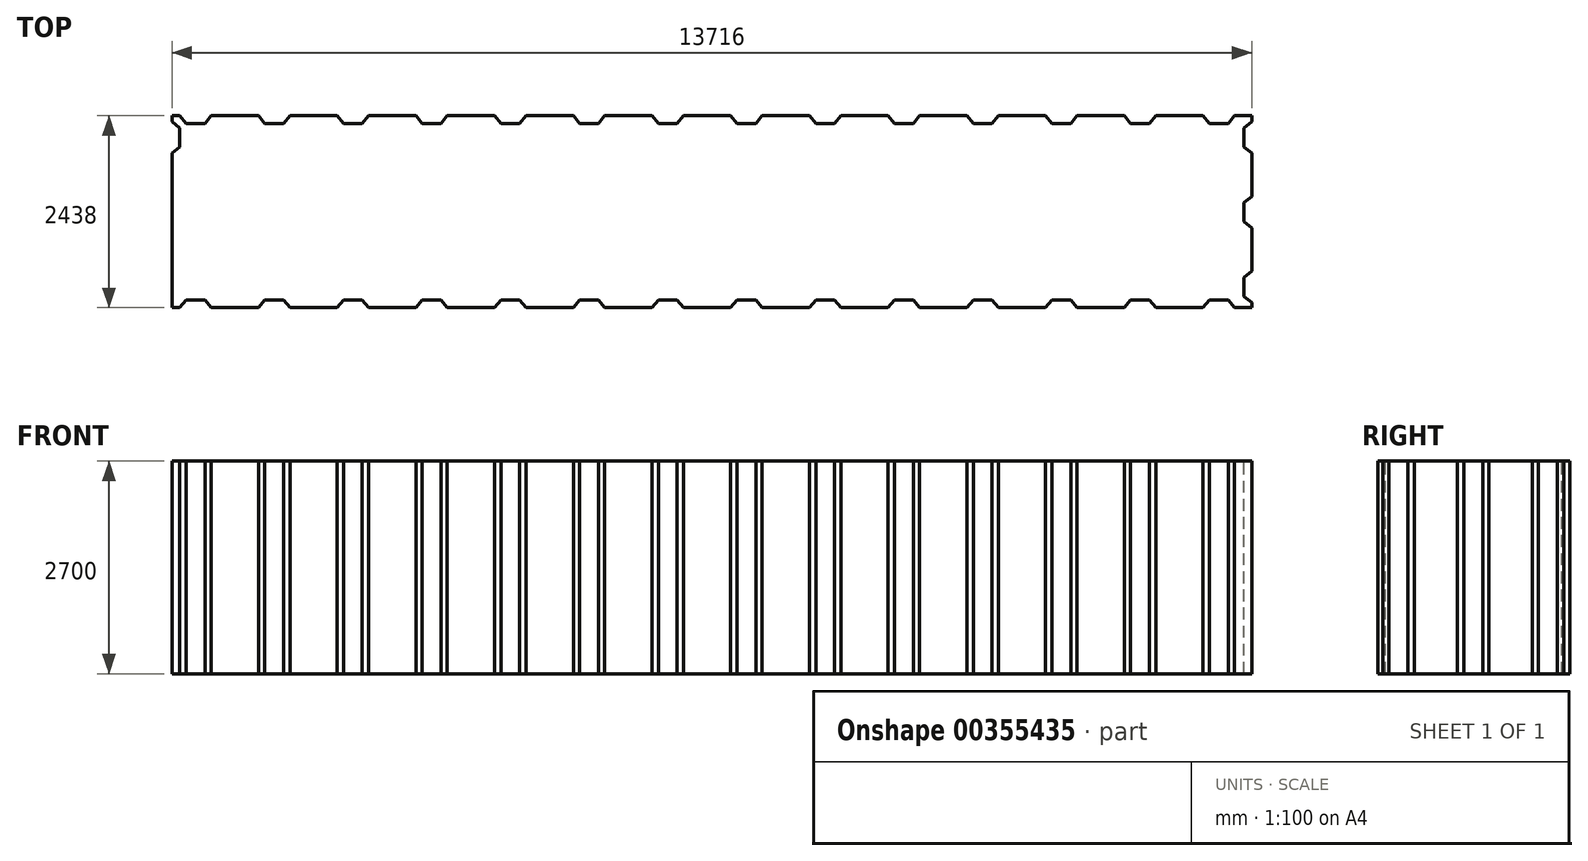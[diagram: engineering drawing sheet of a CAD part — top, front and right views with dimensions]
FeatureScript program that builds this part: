
annotation { "Feature Type Name" : "Feature", "Feature Type Description" : "" }
export const myFeature = defineFeature(function(context is Context, id is Id, definition is map)
    precondition{}
    {
        {
            var Q0;
            Q0=qCreatedBy(makeId("Top.planeOp"),FACE);
            var sketch = newSketch(context, id + "F0", { "sketchPlane" : qUnion([Q0])});
            skLineSegment(sketch, "E0.bottom", {"start": v(6858, -1219) * mm, "end": v(-6858, -1219) * mm});
            skLineSegment(sketch, "E0.top", {"start": v(6858, 1219) * mm, "end": v(-6858, 1219) * mm});
            skLineSegment(sketch, "E0.left", {"start": v(6858, -1219) * mm, "end": v(6858, 1219) * mm});
            skLineSegment(sketch, "E0.right", {"start": v(-6858, -1219) * mm, "end": v(-6858, 1219) * mm});
            skPoint(sketch, "E0.middle", {"position": v(0, 0) * mm});
            skSolve(sketch);
        }
        {
            var Q0;
            Q0=makeQuery(id+"F0.imprint","IMPRINT",FACE,{"disambiguationData":[TD([[makeQuery(id+"F0.imprint","IMPRINT",EDGE,{"derivedFrom":sQuery(id+"F0.wireOp",EDGE,"E0.bottom")}),-1.0]])]});
            extrude(context, id + "F1", {"entities" : qUnion([Q0]), "depth" : 2700 * mm});
        }
        {
            var Q0;
            Q0=makeQuery(id+"F1.opExtrude","CAP_FACE",FACE,{"disambiguationData":[OSD([sQuery(id+"F0.wireOp",EDGE,"E0.bottom"),sQuery(id+"F0.wireOp",EDGE,"E0.top"),sQuery(id+"F0.wireOp",EDGE,"E0.left"),sQuery(id+"F0.wireOp",EDGE,"E0.right")])],"isStart":false});
            var sketch = newSketch(context, id + "F2", { "sketchPlane" : qUnion([Q0])});
            skLineSegment(sketch, "E1", {"start": v(-6760, 1219) * mm, "end": v(-6680, 1119) * mm});
            skLineSegment(sketch, "E2", {"start": v(-6680, 1119) * mm, "end": v(-6560, 1119) * mm});
            skLineSegment(sketch, "E3", {"start": v(-6560, 1119) * mm, "end": v(-6560, 1219) * mm, "construction": true});
            skLineSegment(sketch, "E4", {"start": v(-6560, 1219) * mm, "end": v(-6760, 1219) * mm});
            skLineSegment(sketch, "E5.MirrorCS", {"start": v(-6440, 1119) * mm, "end": v(-6560, 1119) * mm});
            skLineSegment(sketch, "E6.MirrorCS", {"start": v(-6360, 1219) * mm, "end": v(-6440, 1119) * mm});
            skLineSegment(sketch, "E7.MirrorCS", {"start": v(-6560, 1219) * mm, "end": v(-6360, 1219) * mm});
            skLineSegment(sketch, "E8.1.0.0", {"start": v(-5680, 1119) * mm, "end": v(-5560, 1119) * mm});
            skLineSegment(sketch, "E8.1.0.1", {"start": v(-5560, 1219) * mm, "end": v(-5360, 1219) * mm});
            skLineSegment(sketch, "E8.1.0.2", {"start": v(-5360, 1219) * mm, "end": v(-5440, 1119) * mm});
            skLineSegment(sketch, "E8.1.0.3", {"start": v(-5560, 1219) * mm, "end": v(-5760, 1219) * mm});
            skLineSegment(sketch, "E8.1.0.4", {"start": v(-5560, 1119) * mm, "end": v(-5560, 1219) * mm, "construction": true});
            skLineSegment(sketch, "E8.1.0.5", {"start": v(-5440, 1119) * mm, "end": v(-5560, 1119) * mm});
            skLineSegment(sketch, "E8.1.0.6", {"start": v(-5760, 1219) * mm, "end": v(-5680, 1119) * mm});
            skLineSegment(sketch, "E8.2.0.0", {"start": v(-4680, 1119) * mm, "end": v(-4560, 1119) * mm});
            skLineSegment(sketch, "E8.2.0.1", {"start": v(-4560, 1219) * mm, "end": v(-4360, 1219) * mm});
            skLineSegment(sketch, "E8.2.0.2", {"start": v(-4360, 1219) * mm, "end": v(-4440, 1119) * mm});
            skLineSegment(sketch, "E8.2.0.3", {"start": v(-4560, 1219) * mm, "end": v(-4760, 1219) * mm});
            skLineSegment(sketch, "E8.2.0.4", {"start": v(-4560, 1119) * mm, "end": v(-4560, 1219) * mm, "construction": true});
            skLineSegment(sketch, "E8.2.0.5", {"start": v(-4440, 1119) * mm, "end": v(-4560, 1119) * mm});
            skLineSegment(sketch, "E8.2.0.6", {"start": v(-4760, 1219) * mm, "end": v(-4680, 1119) * mm});
            skLineSegment(sketch, "E8.3.0.0", {"start": v(-3680, 1119) * mm, "end": v(-3560, 1119) * mm});
            skLineSegment(sketch, "E8.3.0.1", {"start": v(-3560, 1219) * mm, "end": v(-3360, 1219) * mm});
            skLineSegment(sketch, "E8.3.0.2", {"start": v(-3360, 1219) * mm, "end": v(-3440, 1119) * mm});
            skLineSegment(sketch, "E8.3.0.3", {"start": v(-3560, 1219) * mm, "end": v(-3760, 1219) * mm});
            skLineSegment(sketch, "E8.3.0.4", {"start": v(-3560, 1119) * mm, "end": v(-3560, 1219) * mm, "construction": true});
            skLineSegment(sketch, "E8.3.0.5", {"start": v(-3440, 1119) * mm, "end": v(-3560, 1119) * mm});
            skLineSegment(sketch, "E8.3.0.6", {"start": v(-3760, 1219) * mm, "end": v(-3680, 1119) * mm});
            skLineSegment(sketch, "E8.4.0.0", {"start": v(-2680, 1119) * mm, "end": v(-2560, 1119) * mm});
            skLineSegment(sketch, "E8.4.0.1", {"start": v(-2560, 1219) * mm, "end": v(-2360, 1219) * mm});
            skLineSegment(sketch, "E8.4.0.2", {"start": v(-2360, 1219) * mm, "end": v(-2440, 1119) * mm});
            skLineSegment(sketch, "E8.4.0.3", {"start": v(-2560, 1219) * mm, "end": v(-2760, 1219) * mm});
            skLineSegment(sketch, "E8.4.0.4", {"start": v(-2560, 1119) * mm, "end": v(-2560, 1219) * mm, "construction": true});
            skLineSegment(sketch, "E8.4.0.5", {"start": v(-2440, 1119) * mm, "end": v(-2560, 1119) * mm});
            skLineSegment(sketch, "E8.4.0.6", {"start": v(-2760, 1219) * mm, "end": v(-2680, 1119) * mm});
            skLineSegment(sketch, "E8.5.0.0", {"start": v(-1680, 1119) * mm, "end": v(-1560, 1119) * mm});
            skLineSegment(sketch, "E8.5.0.1", {"start": v(-1560, 1219) * mm, "end": v(-1360, 1219) * mm});
            skLineSegment(sketch, "E8.5.0.2", {"start": v(-1360, 1219) * mm, "end": v(-1440, 1119) * mm});
            skLineSegment(sketch, "E8.5.0.3", {"start": v(-1560, 1219) * mm, "end": v(-1760, 1219) * mm});
            skLineSegment(sketch, "E8.5.0.4", {"start": v(-1560, 1119) * mm, "end": v(-1560, 1219) * mm, "construction": true});
            skLineSegment(sketch, "E8.5.0.5", {"start": v(-1440, 1119) * mm, "end": v(-1560, 1119) * mm});
            skLineSegment(sketch, "E8.5.0.6", {"start": v(-1760, 1219) * mm, "end": v(-1680, 1119) * mm});
            skLineSegment(sketch, "E8.6.0.0", {"start": v(-680, 1119) * mm, "end": v(-560, 1119) * mm});
            skLineSegment(sketch, "E8.6.0.1", {"start": v(-560, 1219) * mm, "end": v(-360, 1219) * mm});
            skLineSegment(sketch, "E8.6.0.2", {"start": v(-360, 1219) * mm, "end": v(-440, 1119) * mm});
            skLineSegment(sketch, "E8.6.0.3", {"start": v(-560, 1219) * mm, "end": v(-760, 1219) * mm});
            skLineSegment(sketch, "E8.6.0.4", {"start": v(-560, 1119) * mm, "end": v(-560, 1219) * mm, "construction": true});
            skLineSegment(sketch, "E8.6.0.5", {"start": v(-440, 1119) * mm, "end": v(-560, 1119) * mm});
            skLineSegment(sketch, "E8.6.0.6", {"start": v(-760, 1219) * mm, "end": v(-680, 1119) * mm});
            skLineSegment(sketch, "E8.7.0.0", {"start": v(320, 1119) * mm, "end": v(440, 1119) * mm});
            skLineSegment(sketch, "E8.7.0.1", {"start": v(440, 1219) * mm, "end": v(640, 1219) * mm});
            skLineSegment(sketch, "E8.7.0.2", {"start": v(640, 1219) * mm, "end": v(560, 1119) * mm});
            skLineSegment(sketch, "E8.7.0.3", {"start": v(440, 1219) * mm, "end": v(240, 1219) * mm});
            skLineSegment(sketch, "E8.7.0.4", {"start": v(440, 1119) * mm, "end": v(440, 1219) * mm, "construction": true});
            skLineSegment(sketch, "E8.7.0.5", {"start": v(560, 1119) * mm, "end": v(440, 1119) * mm});
            skLineSegment(sketch, "E8.7.0.6", {"start": v(240, 1219) * mm, "end": v(320, 1119) * mm});
            skLineSegment(sketch, "E8.8.0.0", {"start": v(1320, 1119) * mm, "end": v(1440, 1119) * mm});
            skLineSegment(sketch, "E8.8.0.1", {"start": v(1440, 1219) * mm, "end": v(1640, 1219) * mm});
            skLineSegment(sketch, "E8.8.0.2", {"start": v(1640, 1219) * mm, "end": v(1560, 1119) * mm});
            skLineSegment(sketch, "E8.8.0.3", {"start": v(1440, 1219) * mm, "end": v(1240, 1219) * mm});
            skLineSegment(sketch, "E8.8.0.4", {"start": v(1440, 1119) * mm, "end": v(1440, 1219) * mm, "construction": true});
            skLineSegment(sketch, "E8.8.0.5", {"start": v(1560, 1119) * mm, "end": v(1440, 1119) * mm});
            skLineSegment(sketch, "E8.8.0.6", {"start": v(1240, 1219) * mm, "end": v(1320, 1119) * mm});
            skLineSegment(sketch, "E8.9.0.0", {"start": v(2320, 1119) * mm, "end": v(2440, 1119) * mm});
            skLineSegment(sketch, "E8.9.0.1", {"start": v(2440, 1219) * mm, "end": v(2640, 1219) * mm});
            skLineSegment(sketch, "E8.9.0.2", {"start": v(2640, 1219) * mm, "end": v(2560, 1119) * mm});
            skLineSegment(sketch, "E8.9.0.3", {"start": v(2440, 1219) * mm, "end": v(2240, 1219) * mm});
            skLineSegment(sketch, "E8.9.0.4", {"start": v(2440, 1119) * mm, "end": v(2440, 1219) * mm, "construction": true});
            skLineSegment(sketch, "E8.9.0.5", {"start": v(2560, 1119) * mm, "end": v(2440, 1119) * mm});
            skLineSegment(sketch, "E8.9.0.6", {"start": v(2240, 1219) * mm, "end": v(2320, 1119) * mm});
            skLineSegment(sketch, "E8.10.0.0", {"start": v(3320, 1119) * mm, "end": v(3440, 1119) * mm});
            skLineSegment(sketch, "E8.10.0.1", {"start": v(3440, 1219) * mm, "end": v(3640, 1219) * mm});
            skLineSegment(sketch, "E8.10.0.2", {"start": v(3640, 1219) * mm, "end": v(3560, 1119) * mm});
            skLineSegment(sketch, "E8.10.0.3", {"start": v(3440, 1219) * mm, "end": v(3240, 1219) * mm});
            skLineSegment(sketch, "E8.10.0.4", {"start": v(3440, 1119) * mm, "end": v(3440, 1219) * mm, "construction": true});
            skLineSegment(sketch, "E8.10.0.5", {"start": v(3560, 1119) * mm, "end": v(3440, 1119) * mm});
            skLineSegment(sketch, "E8.10.0.6", {"start": v(3240, 1219) * mm, "end": v(3320, 1119) * mm});
            skLineSegment(sketch, "E8.11.0.0", {"start": v(4320, 1119) * mm, "end": v(4440, 1119) * mm});
            skLineSegment(sketch, "E8.11.0.1", {"start": v(4440, 1219) * mm, "end": v(4640, 1219) * mm});
            skLineSegment(sketch, "E8.11.0.2", {"start": v(4640, 1219) * mm, "end": v(4560, 1119) * mm});
            skLineSegment(sketch, "E8.11.0.3", {"start": v(4440, 1219) * mm, "end": v(4240, 1219) * mm});
            skLineSegment(sketch, "E8.11.0.4", {"start": v(4440, 1119) * mm, "end": v(4440, 1219) * mm, "construction": true});
            skLineSegment(sketch, "E8.11.0.5", {"start": v(4560, 1119) * mm, "end": v(4440, 1119) * mm});
            skLineSegment(sketch, "E8.11.0.6", {"start": v(4240, 1219) * mm, "end": v(4320, 1119) * mm});
            skLineSegment(sketch, "E8.12.0.0", {"start": v(5320, 1119) * mm, "end": v(5440, 1119) * mm});
            skLineSegment(sketch, "E8.12.0.1", {"start": v(5440, 1219) * mm, "end": v(5640, 1219) * mm});
            skLineSegment(sketch, "E8.12.0.2", {"start": v(5640, 1219) * mm, "end": v(5560, 1119) * mm});
            skLineSegment(sketch, "E8.12.0.3", {"start": v(5440, 1219) * mm, "end": v(5240, 1219) * mm});
            skLineSegment(sketch, "E8.12.0.4", {"start": v(5440, 1119) * mm, "end": v(5440, 1219) * mm, "construction": true});
            skLineSegment(sketch, "E8.12.0.5", {"start": v(5560, 1119) * mm, "end": v(5440, 1119) * mm});
            skLineSegment(sketch, "E8.12.0.6", {"start": v(5240, 1219) * mm, "end": v(5320, 1119) * mm});
            skLineSegment(sketch, "E8.13.0.0", {"start": v(6320, 1119) * mm, "end": v(6440, 1119) * mm});
            skLineSegment(sketch, "E8.13.0.1", {"start": v(6440, 1219) * mm, "end": v(6640, 1219) * mm});
            skLineSegment(sketch, "E8.13.0.2", {"start": v(6640, 1219) * mm, "end": v(6560, 1119) * mm});
            skLineSegment(sketch, "E8.13.0.3", {"start": v(6440, 1219) * mm, "end": v(6240, 1219) * mm});
            skLineSegment(sketch, "E8.13.0.4", {"start": v(6440, 1119) * mm, "end": v(6440, 1219) * mm, "construction": true});
            skLineSegment(sketch, "E8.13.0.5", {"start": v(6560, 1119) * mm, "end": v(6440, 1119) * mm});
            skLineSegment(sketch, "E8.13.0.6", {"start": v(6240, 1219) * mm, "end": v(6320, 1119) * mm});
            skLineSegment(sketch, "E8.direction1", {"start": v(-6680, 1119) * mm, "end": v(-5680, 1119) * mm, "construction": true});
            skLineSegment(sketch, "E9", {"start": v(-7414.32, 0) * mm, "end": v(7419.28, 0) * mm, "construction": true});
            skPoint(sketch, "E9.startSnap0", {"position": v(-6858, 0) * mm});
            skPoint(sketch, "E9.endSnap0", {"position": v(6858, 0) * mm});
            skLineSegment(sketch, "E10.MirrorCS", {"start": v(-1560, -1219) * mm, "end": v(-1360, -1219) * mm});
            skLineSegment(sketch, "E11.MirrorCS", {"start": v(6440, -1219) * mm, "end": v(6640, -1219) * mm});
            skLineSegment(sketch, "E12.MirrorCS", {"start": v(6440, -1219) * mm, "end": v(6240, -1219) * mm});
            skLineSegment(sketch, "E13.MirrorCS", {"start": v(-1560, -1219) * mm, "end": v(-1760, -1219) * mm});
            skLineSegment(sketch, "E14.MirrorCS", {"start": v(6440, -1119) * mm, "end": v(6440, -1219) * mm, "construction": true});
            skLineSegment(sketch, "E15.MirrorCS", {"start": v(-1560, -1119) * mm, "end": v(-1560, -1219) * mm, "construction": true});
            skLineSegment(sketch, "E16.MirrorCS", {"start": v(1560, -1119) * mm, "end": v(1440, -1119) * mm});
            skLineSegment(sketch, "E17.MirrorCS", {"start": v(4320, -1119) * mm, "end": v(4440, -1119) * mm});
            skLineSegment(sketch, "E18.MirrorCS", {"start": v(-3680, -1119) * mm, "end": v(-3560, -1119) * mm});
            skLineSegment(sketch, "E19.MirrorCS", {"start": v(-440, -1119) * mm, "end": v(-560, -1119) * mm});
            skLineSegment(sketch, "E20.MirrorCS", {"start": v(3440, -1219) * mm, "end": v(3640, -1219) * mm});
            skLineSegment(sketch, "E21.MirrorCS", {"start": v(1320, -1119) * mm, "end": v(1440, -1119) * mm});
            skLineSegment(sketch, "E22.MirrorCS", {"start": v(-4560, -1219) * mm, "end": v(-4760, -1219) * mm});
            skLineSegment(sketch, "E23.MirrorCS", {"start": v(-6440, -1119) * mm, "end": v(-6560, -1119) * mm});
            skLineSegment(sketch, "E24.MirrorCS", {"start": v(-3440, -1119) * mm, "end": v(-3560, -1119) * mm});
            skLineSegment(sketch, "E25.MirrorCS", {"start": v(-6560, -1119) * mm, "end": v(-6560, -1219) * mm, "construction": true});
            skLineSegment(sketch, "E26.MirrorCS", {"start": v(-6560, -1219) * mm, "end": v(-6760, -1219) * mm});
            skLineSegment(sketch, "E27.MirrorCS", {"start": v(-4560, -1219) * mm, "end": v(-4360, -1219) * mm});
            skLineSegment(sketch, "E28.MirrorCS", {"start": v(-680, -1119) * mm, "end": v(-560, -1119) * mm});
            skLineSegment(sketch, "E29.MirrorCS", {"start": v(4560, -1119) * mm, "end": v(4440, -1119) * mm});
            skLineSegment(sketch, "E30.MirrorCS", {"start": v(-6760, -1219) * mm, "end": v(-6680, -1119) * mm});
            skLineSegment(sketch, "E31.MirrorCS", {"start": v(-6560, -1219) * mm, "end": v(-6360, -1219) * mm});
            skLineSegment(sketch, "E32.MirrorCS", {"start": v(-4560, -1119) * mm, "end": v(-4560, -1219) * mm, "construction": true});
            skLineSegment(sketch, "E33.MirrorCS", {"start": v(3440, -1219) * mm, "end": v(3240, -1219) * mm});
            skLineSegment(sketch, "E34.MirrorCS", {"start": v(3440, -1119) * mm, "end": v(3440, -1219) * mm, "construction": true});
            skLineSegment(sketch, "E35.MirrorCS", {"start": v(-6680, -1119) * mm, "end": v(-6560, -1119) * mm});
            skLineSegment(sketch, "E36.MirrorCS", {"start": v(440, -1219) * mm, "end": v(240, -1219) * mm});
            skLineSegment(sketch, "E37.MirrorCS", {"start": v(-560, -1219) * mm, "end": v(-760, -1219) * mm});
            skLineSegment(sketch, "E38.MirrorCS", {"start": v(2560, -1119) * mm, "end": v(2440, -1119) * mm});
            skLineSegment(sketch, "E39.MirrorCS", {"start": v(5320, -1119) * mm, "end": v(5440, -1119) * mm});
            skLineSegment(sketch, "E40.MirrorCS", {"start": v(1440, -1119) * mm, "end": v(1440, -1219) * mm, "construction": true});
            skLineSegment(sketch, "E41.MirrorCS", {"start": v(-2680, -1119) * mm, "end": v(-2560, -1119) * mm});
            skLineSegment(sketch, "E42.MirrorCS", {"start": v(4440, -1219) * mm, "end": v(4640, -1219) * mm});
            skLineSegment(sketch, "E43.MirrorCS", {"start": v(5440, -1219) * mm, "end": v(5640, -1219) * mm});
            skLineSegment(sketch, "E44.MirrorCS", {"start": v(-560, -1119) * mm, "end": v(-560, -1219) * mm, "construction": true});
            skLineSegment(sketch, "E45.MirrorCS", {"start": v(440, -1119) * mm, "end": v(440, -1219) * mm, "construction": true});
            skLineSegment(sketch, "E46.MirrorCS", {"start": v(-2560, -1219) * mm, "end": v(-2760, -1219) * mm});
            skLineSegment(sketch, "E47.MirrorCS", {"start": v(-3560, -1219) * mm, "end": v(-3360, -1219) * mm});
            skLineSegment(sketch, "E48.MirrorCS", {"start": v(2320, -1119) * mm, "end": v(2440, -1119) * mm});
            skLineSegment(sketch, "E49.MirrorCS", {"start": v(3320, -1119) * mm, "end": v(3440, -1119) * mm});
            skLineSegment(sketch, "E50.MirrorCS", {"start": v(560, -1119) * mm, "end": v(440, -1119) * mm});
            skLineSegment(sketch, "E51.MirrorCS", {"start": v(6560, -1119) * mm, "end": v(6440, -1119) * mm});
            skLineSegment(sketch, "E52.MirrorCS", {"start": v(4440, -1219) * mm, "end": v(4240, -1219) * mm});
            skLineSegment(sketch, "E53.MirrorCS", {"start": v(2440, -1219) * mm, "end": v(2640, -1219) * mm});
            skLineSegment(sketch, "E54.MirrorCS", {"start": v(3560, -1119) * mm, "end": v(3440, -1119) * mm});
            skLineSegment(sketch, "E55.MirrorCS", {"start": v(-2560, -1119) * mm, "end": v(-2560, -1219) * mm, "construction": true});
            skLineSegment(sketch, "E56.MirrorCS", {"start": v(5440, -1219) * mm, "end": v(5240, -1219) * mm});
            skLineSegment(sketch, "E57.MirrorCS", {"start": v(-1440, -1119) * mm, "end": v(-1560, -1119) * mm});
            skLineSegment(sketch, "E58.MirrorCS", {"start": v(-3560, -1219) * mm, "end": v(-3760, -1219) * mm});
            skLineSegment(sketch, "E59.MirrorCS", {"start": v(5440, -1119) * mm, "end": v(5440, -1219) * mm, "construction": true});
            skLineSegment(sketch, "E60.MirrorCS", {"start": v(-2440, -1119) * mm, "end": v(-2560, -1119) * mm});
            skLineSegment(sketch, "E61.MirrorCS", {"start": v(2440, -1219) * mm, "end": v(2240, -1219) * mm});
            skLineSegment(sketch, "E62.MirrorCS", {"start": v(-5560, -1219) * mm, "end": v(-5360, -1219) * mm});
            skLineSegment(sketch, "E63.MirrorCS", {"start": v(320, -1119) * mm, "end": v(440, -1119) * mm});
            skLineSegment(sketch, "E64.MirrorCS", {"start": v(-5560, -1219) * mm, "end": v(-5760, -1219) * mm});
            skLineSegment(sketch, "E65.MirrorCS", {"start": v(-1680, -1119) * mm, "end": v(-1560, -1119) * mm});
            skLineSegment(sketch, "E66.MirrorCS", {"start": v(-5440, -1119) * mm, "end": v(-5560, -1119) * mm});
            skLineSegment(sketch, "E67.MirrorCS", {"start": v(-4680, -1119) * mm, "end": v(-4560, -1119) * mm});
            skLineSegment(sketch, "E68.MirrorCS", {"start": v(-3560, -1119) * mm, "end": v(-3560, -1219) * mm, "construction": true});
            skLineSegment(sketch, "E69.MirrorCS", {"start": v(-5760, -1219) * mm, "end": v(-5680, -1119) * mm});
            skLineSegment(sketch, "E70.MirrorCS", {"start": v(-2560, -1219) * mm, "end": v(-2360, -1219) * mm});
            skLineSegment(sketch, "E71.MirrorCS", {"start": v(440, -1219) * mm, "end": v(640, -1219) * mm});
            skLineSegment(sketch, "E72.MirrorCS", {"start": v(-5680, -1119) * mm, "end": v(-5560, -1119) * mm});
            skLineSegment(sketch, "E73.MirrorCS", {"start": v(-560, -1219) * mm, "end": v(-360, -1219) * mm});
            skLineSegment(sketch, "E74.MirrorCS", {"start": v(1440, -1219) * mm, "end": v(1240, -1219) * mm});
            skLineSegment(sketch, "E75.MirrorCS", {"start": v(1440, -1219) * mm, "end": v(1640, -1219) * mm});
            skLineSegment(sketch, "E76.MirrorCS", {"start": v(6320, -1119) * mm, "end": v(6440, -1119) * mm});
            skLineSegment(sketch, "E77.MirrorCS", {"start": v(-4440, -1119) * mm, "end": v(-4560, -1119) * mm});
            skLineSegment(sketch, "E78.MirrorCS", {"start": v(-6360, -1219) * mm, "end": v(-6440, -1119) * mm});
            skLineSegment(sketch, "E79.MirrorCS", {"start": v(-5560, -1119) * mm, "end": v(-5560, -1219) * mm, "construction": true});
            skLineSegment(sketch, "E80.MirrorCS", {"start": v(4440, -1119) * mm, "end": v(4440, -1219) * mm, "construction": true});
            skLineSegment(sketch, "E81.MirrorCS", {"start": v(-6680, -1119) * mm, "end": v(-5680, -1119) * mm, "construction": true});
            skLineSegment(sketch, "E82.MirrorCS", {"start": v(2440, -1119) * mm, "end": v(2440, -1219) * mm, "construction": true});
            skLineSegment(sketch, "E83.MirrorCS", {"start": v(5560, -1119) * mm, "end": v(5440, -1119) * mm});
            skLineSegment(sketch, "E84.MirrorCS", {"start": v(-4760, -1219) * mm, "end": v(-4680, -1119) * mm});
            skLineSegment(sketch, "E85.MirrorCS", {"start": v(6640, -1219) * mm, "end": v(6560, -1119) * mm});
            skLineSegment(sketch, "E86.MirrorCS", {"start": v(3240, -1219) * mm, "end": v(3320, -1119) * mm});
            skLineSegment(sketch, "E87.MirrorCS", {"start": v(-360, -1219) * mm, "end": v(-440, -1119) * mm});
            skLineSegment(sketch, "E88.MirrorCS", {"start": v(-2360, -1219) * mm, "end": v(-2440, -1119) * mm});
            skLineSegment(sketch, "E89.MirrorCS", {"start": v(-1360, -1219) * mm, "end": v(-1440, -1119) * mm});
            skLineSegment(sketch, "E90.MirrorCS", {"start": v(2240, -1219) * mm, "end": v(2320, -1119) * mm});
            skLineSegment(sketch, "E91.MirrorCS", {"start": v(1240, -1219) * mm, "end": v(1320, -1119) * mm});
            skLineSegment(sketch, "E92.MirrorCS", {"start": v(4640, -1219) * mm, "end": v(4560, -1119) * mm});
            skLineSegment(sketch, "E93.MirrorCS", {"start": v(5640, -1219) * mm, "end": v(5560, -1119) * mm});
            skLineSegment(sketch, "E94.MirrorCS", {"start": v(-760, -1219) * mm, "end": v(-680, -1119) * mm});
            skLineSegment(sketch, "E95.MirrorCS", {"start": v(240, -1219) * mm, "end": v(320, -1119) * mm});
            skLineSegment(sketch, "E96.MirrorCS", {"start": v(-3360, -1219) * mm, "end": v(-3440, -1119) * mm});
            skLineSegment(sketch, "E97.MirrorCS", {"start": v(-4360, -1219) * mm, "end": v(-4440, -1119) * mm});
            skLineSegment(sketch, "E98.MirrorCS", {"start": v(3640, -1219) * mm, "end": v(3560, -1119) * mm});
            skLineSegment(sketch, "E99.MirrorCS", {"start": v(6240, -1219) * mm, "end": v(6320, -1119) * mm});
            skLineSegment(sketch, "E100.MirrorCS", {"start": v(4240, -1219) * mm, "end": v(4320, -1119) * mm});
            skLineSegment(sketch, "E101.MirrorCS", {"start": v(-3760, -1219) * mm, "end": v(-3680, -1119) * mm});
            skLineSegment(sketch, "E102.MirrorCS", {"start": v(2640, -1219) * mm, "end": v(2560, -1119) * mm});
            skLineSegment(sketch, "E103.MirrorCS", {"start": v(640, -1219) * mm, "end": v(560, -1119) * mm});
            skLineSegment(sketch, "E104.MirrorCS", {"start": v(5240, -1219) * mm, "end": v(5320, -1119) * mm});
            skLineSegment(sketch, "E105.MirrorCS", {"start": v(1640, -1219) * mm, "end": v(1560, -1119) * mm});
            skLineSegment(sketch, "E106.MirrorCS", {"start": v(-1760, -1219) * mm, "end": v(-1680, -1119) * mm});
            skLineSegment(sketch, "E107.MirrorCS", {"start": v(-2760, -1219) * mm, "end": v(-2680, -1119) * mm});
            skLineSegment(sketch, "E108.MirrorCS", {"start": v(-5360, -1219) * mm, "end": v(-5440, -1119) * mm});
            skLineSegment(sketch, "E109", {"start": v(-6858, 944) * mm, "end": v(-6858, 1144) * mm});
            skLineSegment(sketch, "E110", {"start": v(-6858, 1144) * mm, "end": v(-6758, 1064) * mm});
            skLineSegment(sketch, "E111", {"start": v(-6758, 1064) * mm, "end": v(-6758, 944) * mm});
            skLineSegment(sketch, "E112", {"start": v(-6758, 944) * mm, "end": v(-6858, 944) * mm, "construction": true});
            skLineSegment(sketch, "E113.MirrorCS", {"start": v(-6858, 944) * mm, "end": v(-6858, 744) * mm});
            skLineSegment(sketch, "E114.MirrorCS", {"start": v(-6858, 744) * mm, "end": v(-6758, 824) * mm});
            skLineSegment(sketch, "E115.MirrorCS", {"start": v(-6758, 824) * mm, "end": v(-6758, 944) * mm});
            skLineSegment(sketch, "E116.0.1.0", {"start": v(-6758, -6) * mm, "end": v(-6858, -6) * mm, "construction": true});
            skLineSegment(sketch, "E116.0.1.1", {"start": v(-6758, 114) * mm, "end": v(-6758, -6) * mm});
            skLineSegment(sketch, "E116.0.1.2", {"start": v(-6858, -206) * mm, "end": v(-6758, -126) * mm});
            skLineSegment(sketch, "E116.0.1.3", {"start": v(-6758, -126) * mm, "end": v(-6758, -6) * mm});
            skLineSegment(sketch, "E116.0.1.4", {"start": v(-6858, 194) * mm, "end": v(-6758, 114) * mm});
            skLineSegment(sketch, "E116.0.1.5", {"start": v(-6858, -6) * mm, "end": v(-6858, -206) * mm});
            skLineSegment(sketch, "E116.0.1.6", {"start": v(-6858, -6) * mm, "end": v(-6858, 194) * mm});
            skLineSegment(sketch, "E116.0.1.7", {"start": v(-6758, -126) * mm, "end": v(-6758, -6) * mm});
            skLineSegment(sketch, "E116.0.1.8", {"start": v(-6858, -206) * mm, "end": v(-6758, -126) * mm});
            skLineSegment(sketch, "E116.0.1.9", {"start": v(-6858, -6) * mm, "end": v(-6858, -206) * mm});
            skLineSegment(sketch, "E116.0.1.10", {"start": v(-6858, 194) * mm, "end": v(-6758, 114) * mm});
            skLineSegment(sketch, "E116.0.1.11", {"start": v(-6858, -6) * mm, "end": v(-6858, 194) * mm});
            skLineSegment(sketch, "E116.0.1.12", {"start": v(-6758, 114) * mm, "end": v(-6758, -6) * mm});
            skLineSegment(sketch, "E116.0.1.13", {"start": v(-6858, -6) * mm, "end": v(-6858, -206) * mm});
            skLineSegment(sketch, "E116.0.1.14", {"start": v(-6858, -206) * mm, "end": v(-6758, -126) * mm});
            skLineSegment(sketch, "E116.0.1.15", {"start": v(-6758, -126) * mm, "end": v(-6758, -6) * mm});
            skLineSegment(sketch, "E116.0.1.16", {"start": v(-6858, 194) * mm, "end": v(-6758, 114) * mm});
            skLineSegment(sketch, "E116.0.1.17", {"start": v(-6858, -6) * mm, "end": v(-6858, 194) * mm});
            skLineSegment(sketch, "E116.0.1.18", {"start": v(-6758, 114) * mm, "end": v(-6758, -6) * mm});
            skLineSegment(sketch, "E116.0.1.19", {"start": v(-6858, -6) * mm, "end": v(-6858, -206) * mm});
            skLineSegment(sketch, "E116.0.1.20", {"start": v(-6858, 194) * mm, "end": v(-6758, 114) * mm});
            skLineSegment(sketch, "E116.0.1.21", {"start": v(-6758, -126) * mm, "end": v(-6758, -6) * mm});
            skLineSegment(sketch, "E116.0.1.22", {"start": v(-6858, -206) * mm, "end": v(-6758, -126) * mm});
            skLineSegment(sketch, "E116.0.1.23", {"start": v(-6858, -6) * mm, "end": v(-6858, 194) * mm});
            skLineSegment(sketch, "E116.0.1.24", {"start": v(-6758, 114) * mm, "end": v(-6758, -6) * mm});
            skLineSegment(sketch, "E116.0.2.0", {"start": v(-6758, -956) * mm, "end": v(-6858, -956) * mm, "construction": true});
            skLineSegment(sketch, "E116.0.2.1", {"start": v(-6758, -836) * mm, "end": v(-6758, -956) * mm});
            skLineSegment(sketch, "E116.0.2.2", {"start": v(-6858, -1156) * mm, "end": v(-6758, -1076) * mm});
            skLineSegment(sketch, "E116.0.2.3", {"start": v(-6758, -1076) * mm, "end": v(-6758, -956) * mm});
            skLineSegment(sketch, "E116.0.2.4", {"start": v(-6858, -756) * mm, "end": v(-6758, -836) * mm});
            skLineSegment(sketch, "E116.0.2.5", {"start": v(-6858, -956) * mm, "end": v(-6858, -1156) * mm});
            skLineSegment(sketch, "E116.0.2.6", {"start": v(-6858, -956) * mm, "end": v(-6858, -756) * mm});
            skLineSegment(sketch, "E116.0.2.7", {"start": v(-6758, -1076) * mm, "end": v(-6758, -956) * mm});
            skLineSegment(sketch, "E116.0.2.8", {"start": v(-6858, -1156) * mm, "end": v(-6758, -1076) * mm});
            skLineSegment(sketch, "E116.0.2.9", {"start": v(-6858, -956) * mm, "end": v(-6858, -1156) * mm});
            skLineSegment(sketch, "E116.0.2.10", {"start": v(-6858, -756) * mm, "end": v(-6758, -836) * mm});
            skLineSegment(sketch, "E116.0.2.11", {"start": v(-6858, -956) * mm, "end": v(-6858, -756) * mm});
            skLineSegment(sketch, "E116.0.2.12", {"start": v(-6758, -836) * mm, "end": v(-6758, -956) * mm});
            skLineSegment(sketch, "E116.0.2.13", {"start": v(-6858, -956) * mm, "end": v(-6858, -1156) * mm});
            skLineSegment(sketch, "E116.0.2.14", {"start": v(-6858, -1156) * mm, "end": v(-6758, -1076) * mm});
            skLineSegment(sketch, "E116.0.2.15", {"start": v(-6758, -1076) * mm, "end": v(-6758, -956) * mm});
            skLineSegment(sketch, "E116.0.2.16", {"start": v(-6858, -756) * mm, "end": v(-6758, -836) * mm});
            skLineSegment(sketch, "E116.0.2.17", {"start": v(-6858, -956) * mm, "end": v(-6858, -756) * mm});
            skLineSegment(sketch, "E116.0.2.18", {"start": v(-6758, -836) * mm, "end": v(-6758, -956) * mm});
            skLineSegment(sketch, "E116.0.2.19", {"start": v(-6858, -956) * mm, "end": v(-6858, -1156) * mm});
            skLineSegment(sketch, "E116.0.2.20", {"start": v(-6858, -756) * mm, "end": v(-6758, -836) * mm});
            skLineSegment(sketch, "E116.0.2.21", {"start": v(-6758, -1076) * mm, "end": v(-6758, -956) * mm});
            skLineSegment(sketch, "E116.0.2.22", {"start": v(-6858, -1156) * mm, "end": v(-6758, -1076) * mm});
            skLineSegment(sketch, "E116.0.2.23", {"start": v(-6858, -956) * mm, "end": v(-6858, -756) * mm});
            skLineSegment(sketch, "E116.0.2.24", {"start": v(-6758, -836) * mm, "end": v(-6758, -956) * mm});
            skLineSegment(sketch, "E116.direction1", {"start": v(-6858, 744) * mm, "end": v(-6833, 744) * mm, "construction": true});
            skLineSegment(sketch, "E116.direction2", {"start": v(-6858, 744) * mm, "end": v(-6858, -206) * mm, "construction": true});
            skLineSegment(sketch, "E117", {"start": v(0, 1757.9) * mm, "end": v(0, -1552.38) * mm, "construction": true});
            skLineSegment(sketch, "E118.MirrorCS", {"start": v(6758, 1064) * mm, "end": v(6758, 944) * mm});
            skLineSegment(sketch, "E119.MirrorCS", {"start": v(6758, -836) * mm, "end": v(6758, -956) * mm});
            skLineSegment(sketch, "E120.MirrorCS", {"start": v(6858, 1144) * mm, "end": v(6758, 1064) * mm});
            skLineSegment(sketch, "E121.MirrorCS", {"start": v(6758, 114) * mm, "end": v(6758, -6) * mm});
            skLineSegment(sketch, "E122.MirrorCS", {"start": v(6858, 194) * mm, "end": v(6758, 114) * mm});
            skLineSegment(sketch, "E123.MirrorCS", {"start": v(6758, -126) * mm, "end": v(6758, -6) * mm});
            skLineSegment(sketch, "E124.MirrorCS", {"start": v(6858, -1156) * mm, "end": v(6758, -1076) * mm});
            skLineSegment(sketch, "E125.MirrorCS", {"start": v(6858, -206) * mm, "end": v(6758, -126) * mm});
            skLineSegment(sketch, "E126.MirrorCS", {"start": v(6758, -1076) * mm, "end": v(6758, -956) * mm});
            skLineSegment(sketch, "E127.MirrorCS", {"start": v(6858, 744) * mm, "end": v(6758, 824) * mm});
            skLineSegment(sketch, "E128.MirrorCS", {"start": v(6858, -756) * mm, "end": v(6758, -836) * mm});
            skLineSegment(sketch, "E129.MirrorCS", {"start": v(6758, 824) * mm, "end": v(6758, 944) * mm});
            skLineSegment(sketch, "E130.MirrorCS", {"start": v(6858, 744) * mm, "end": v(6833, 744) * mm, "construction": true});
            skLineSegment(sketch, "E131.MirrorCS", {"start": v(6758, 944) * mm, "end": v(6858, 944) * mm, "construction": true});
            skLineSegment(sketch, "E132.MirrorCS", {"start": v(6758, -956) * mm, "end": v(6858, -956) * mm, "construction": true});
            skLineSegment(sketch, "E133.MirrorCS", {"start": v(6758, -6) * mm, "end": v(6858, -6) * mm, "construction": true});
            skLineSegment(sketch, "E134.MirrorCS", {"start": v(6858, 944) * mm, "end": v(6858, 1144) * mm});
            skLineSegment(sketch, "E135.MirrorCS", {"start": v(6858, -6) * mm, "end": v(6858, 194) * mm});
            skLineSegment(sketch, "E136.MirrorCS", {"start": v(6858, -6) * mm, "end": v(6858, -206) * mm});
            skLineSegment(sketch, "E137.MirrorCS", {"start": v(6858, -956) * mm, "end": v(6858, -756) * mm});
            skLineSegment(sketch, "E138.MirrorCS", {"start": v(6858, -956) * mm, "end": v(6858, -1156) * mm});
            skLineSegment(sketch, "E139.MirrorCS", {"start": v(6858, 944) * mm, "end": v(6858, 744) * mm});
            skLineSegment(sketch, "E140.MirrorCS", {"start": v(6858, 744) * mm, "end": v(6858, -206) * mm, "construction": true});
            skSolve(sketch);
        }
        {
            var Q0;
            Q0=makeQuery(id+"F2.imprint","IMPRINT",FACE,{"disambiguationData":[TD([[makeQuery(id+"F2.imprint","IMPRINT",EDGE,{"derivedFrom":sQuery(id+"F2.wireOp",EDGE,"E1")}),1.0]])]});
            var Q1;
            Q1=makeQuery(id+"F2.imprint","IMPRINT",FACE,{"disambiguationData":[TD([[makeQuery(id+"F2.imprint","IMPRINT",EDGE,{"derivedFrom":sQuery(id+"F2.wireOp",EDGE,"E8.1.0.0")}),1.0]])]});
            var Q2;
            Q2=makeQuery(id+"F2.imprint","IMPRINT",FACE,{"disambiguationData":[TD([[makeQuery(id+"F2.imprint","IMPRINT",EDGE,{"derivedFrom":sQuery(id+"F2.wireOp",EDGE,"E8.2.0.0")}),1.0]])]});
            var Q3;
            Q3=makeQuery(id+"F2.imprint","IMPRINT",FACE,{"disambiguationData":[TD([[makeQuery(id+"F2.imprint","IMPRINT",EDGE,{"derivedFrom":sQuery(id+"F2.wireOp",EDGE,"E23.MirrorCS")}),1.0]])]});
            var Q4;
            Q4=makeQuery(id+"F2.imprint","IMPRINT",FACE,{"disambiguationData":[TD([[makeQuery(id+"F2.imprint","IMPRINT",EDGE,{"derivedFrom":sQuery(id+"F2.wireOp",EDGE,"E62.MirrorCS")}),-1.0]])]});
            var Q5;
            Q5=makeQuery(id+"F2.imprint","IMPRINT",FACE,{"disambiguationData":[TD([[makeQuery(id+"F2.imprint","IMPRINT",EDGE,{"derivedFrom":sQuery(id+"F2.wireOp",EDGE,"E22.MirrorCS")}),-1.0]])]});
            var Q6;
            Q6=makeQuery(id+"F2.imprint","IMPRINT",FACE,{"disambiguationData":[TD([[makeQuery(id+"F2.imprint","IMPRINT",EDGE,{"derivedFrom":sQuery(id+"F2.wireOp",EDGE,"E18.MirrorCS")}),-1.0]])]});
            var Q7;
            Q7=makeQuery(id+"F2.imprint","IMPRINT",FACE,{"disambiguationData":[TD([[makeQuery(id+"F2.imprint","IMPRINT",EDGE,{"derivedFrom":sQuery(id+"F2.wireOp",EDGE,"E41.MirrorCS")}),-1.0]])]});
            var Q8;
            Q8=makeQuery(id+"F2.imprint","IMPRINT",FACE,{"disambiguationData":[TD([[makeQuery(id+"F2.imprint","IMPRINT",EDGE,{"derivedFrom":sQuery(id+"F2.wireOp",EDGE,"E8.4.0.0")}),1.0]])]});
            var Q9;
            Q9=makeQuery(id+"F2.imprint","IMPRINT",FACE,{"disambiguationData":[TD([[makeQuery(id+"F2.imprint","IMPRINT",EDGE,{"derivedFrom":sQuery(id+"F2.wireOp",EDGE,"E8.5.0.0")}),1.0]])]});
            var Q10;
            Q10=makeQuery(id+"F2.imprint","IMPRINT",FACE,{"disambiguationData":[TD([[makeQuery(id+"F2.imprint","IMPRINT",EDGE,{"derivedFrom":sQuery(id+"F2.wireOp",EDGE,"E8.3.0.0")}),1.0]])]});
            var Q11;
            Q11=makeQuery(id+"F2.imprint","IMPRINT",FACE,{"disambiguationData":[TD([[makeQuery(id+"F2.imprint","IMPRINT",EDGE,{"derivedFrom":sQuery(id+"F2.wireOp",EDGE,"E10.MirrorCS")}),-1.0]])]});
            var Q12;
            Q12=makeQuery(id+"F2.imprint","IMPRINT",FACE,{"disambiguationData":[TD([[makeQuery(id+"F2.imprint","IMPRINT",EDGE,{"derivedFrom":sQuery(id+"F2.wireOp",EDGE,"E19.MirrorCS")}),1.0]])]});
            var Q13;
            Q13=makeQuery(id+"F2.imprint","IMPRINT",FACE,{"disambiguationData":[TD([[makeQuery(id+"F2.imprint","IMPRINT",EDGE,{"derivedFrom":sQuery(id+"F2.wireOp",EDGE,"E8.6.0.0")}),1.0]])]});
            var Q14;
            Q14=makeQuery(id+"F2.imprint","IMPRINT",FACE,{"disambiguationData":[TD([[makeQuery(id+"F2.imprint","IMPRINT",EDGE,{"derivedFrom":sQuery(id+"F2.wireOp",EDGE,"E8.7.0.0")}),1.0]])]});
            var Q15;
            Q15=makeQuery(id+"F2.imprint","IMPRINT",FACE,{"disambiguationData":[TD([[makeQuery(id+"F2.imprint","IMPRINT",EDGE,{"derivedFrom":sQuery(id+"F2.wireOp",EDGE,"E8.8.0.0")}),1.0]])]});
            var Q16;
            Q16=makeQuery(id+"F2.imprint","IMPRINT",FACE,{"disambiguationData":[TD([[makeQuery(id+"F2.imprint","IMPRINT",EDGE,{"derivedFrom":sQuery(id+"F2.wireOp",EDGE,"E36.MirrorCS")}),-1.0]])]});
            var Q17;
            Q17=makeQuery(id+"F2.imprint","IMPRINT",FACE,{"disambiguationData":[TD([[makeQuery(id+"F2.imprint","IMPRINT",EDGE,{"derivedFrom":sQuery(id+"F2.wireOp",EDGE,"E16.MirrorCS")}),1.0]])]});
            var Q18;
            Q18=makeQuery(id+"F2.imprint","IMPRINT",FACE,{"disambiguationData":[TD([[makeQuery(id+"F2.imprint","IMPRINT",EDGE,{"derivedFrom":sQuery(id+"F2.wireOp",EDGE,"E38.MirrorCS")}),1.0]])]});
            var Q19;
            Q19=makeQuery(id+"F2.imprint","IMPRINT",FACE,{"disambiguationData":[TD([[makeQuery(id+"F2.imprint","IMPRINT",EDGE,{"derivedFrom":sQuery(id+"F2.wireOp",EDGE,"E8.9.0.0")}),1.0]])]});
            var Q20;
            Q20=makeQuery(id+"F2.imprint","IMPRINT",FACE,{"disambiguationData":[TD([[makeQuery(id+"F2.imprint","IMPRINT",EDGE,{"derivedFrom":sQuery(id+"F2.wireOp",EDGE,"E8.10.0.0")}),1.0]])]});
            var Q21;
            Q21=makeQuery(id+"F2.imprint","IMPRINT",FACE,{"disambiguationData":[TD([[makeQuery(id+"F2.imprint","IMPRINT",EDGE,{"derivedFrom":sQuery(id+"F2.wireOp",EDGE,"E8.11.0.0")}),1.0]])]});
            var Q22;
            Q22=makeQuery(id+"F2.imprint","IMPRINT",FACE,{"disambiguationData":[TD([[makeQuery(id+"F2.imprint","IMPRINT",EDGE,{"derivedFrom":sQuery(id+"F2.wireOp",EDGE,"E8.12.0.0")}),1.0]])]});
            var Q23;
            Q23=makeQuery(id+"F2.imprint","IMPRINT",FACE,{"disambiguationData":[TD([[makeQuery(id+"F2.imprint","IMPRINT",EDGE,{"derivedFrom":sQuery(id+"F2.wireOp",EDGE,"E39.MirrorCS")}),-1.0]])]});
            var Q24;
            Q24=makeQuery(id+"F2.imprint","IMPRINT",FACE,{"disambiguationData":[TD([[makeQuery(id+"F2.imprint","IMPRINT",EDGE,{"derivedFrom":sQuery(id+"F2.wireOp",EDGE,"E17.MirrorCS")}),-1.0]])]});
            var Q25;
            Q25=makeQuery(id+"F2.imprint","IMPRINT",FACE,{"disambiguationData":[TD([[makeQuery(id+"F2.imprint","IMPRINT",EDGE,{"derivedFrom":sQuery(id+"F2.wireOp",EDGE,"E20.MirrorCS")}),-1.0]])]});
            var Q26;
            Q26=makeQuery(id+"F2.imprint","IMPRINT",FACE,{"disambiguationData":[TD([[makeQuery(id+"F2.imprint","IMPRINT",EDGE,{"derivedFrom":sQuery(id+"F2.wireOp",EDGE,"E8.13.0.0")}),1.0]])]});
            var Q27;
            Q27=makeQuery(id+"F2.imprint","IMPRINT",FACE,{"disambiguationData":[TD([[makeQuery(id+"F2.imprint","IMPRINT",EDGE,{"derivedFrom":sQuery(id+"F2.wireOp",EDGE,"E11.MirrorCS")}),-1.0]])]});
            var Q28;
            Q28=makeQuery(id+"F2.imprint","IMPRINT",FACE,{"disambiguationData":[TD([[makeQuery(id+"F2.imprint","IMPRINT",EDGE,{"derivedFrom":sQuery(id+"F2.wireOp",EDGE,"E127.MirrorCS")}),-1.0]])]});
            var Q29;
            Q29=makeQuery(id+"F2.imprint","IMPRINT",FACE,{"disambiguationData":[TD([[makeQuery(id+"F2.imprint","IMPRINT",EDGE,{"derivedFrom":sQuery(id+"F2.wireOp",EDGE,"E121.MirrorCS")}),1.0]])]});
            var Q30;
            Q30=makeQuery(id+"F2.imprint","IMPRINT",FACE,{"disambiguationData":[TD([[makeQuery(id+"F2.imprint","IMPRINT",EDGE,{"derivedFrom":sQuery(id+"F2.wireOp",EDGE,"E126.MirrorCS")}),-1.0]])]});
            var Q31;
            Q31=makeQuery(id+"F2.imprint","IMPRINT",FACE,{"disambiguationData":[TD([[makeQuery(id+"F2.imprint","IMPRINT",EDGE,{"derivedFrom":sQuery(id+"F2.wireOp",EDGE,"E111")}),-1.0]])]});
            var Q32;
            Q32=makeQuery(id+"F2.imprint","IMPRINT",FACE,{"disambiguationData":[TD([[makeQuery(id+"F2.imprint","IMPRINT",EDGE,{"derivedFrom":sQuery(id+"F2.wireOp",EDGE,"E116.0.1.19")}),-1.0]])]});
            var Q33;
            Q33=makeQuery(id+"F2.imprint","IMPRINT",FACE,{"disambiguationData":[TD([[makeQuery(id+"F2.imprint","IMPRINT",EDGE,{"derivedFrom":sQuery(id+"F2.wireOp",EDGE,"E116.0.2.19")}),-1.0]])]});
            var Q34;
            Q34=makeQuery(id+"F1.opExtrude","CAP_FACE",FACE,{"disambiguationData":[OSD([sQuery(id+"F0.wireOp",EDGE,"E0.bottom"),sQuery(id+"F0.wireOp",EDGE,"E0.top"),sQuery(id+"F0.wireOp",EDGE,"E0.left"),sQuery(id+"F0.wireOp",EDGE,"E0.right")])],"isStart":true});
            extrude(context, id + "F3", {"entities" : qUnion([Q0, Q1, Q2, Q3, Q4, Q5, Q6, Q7, Q8, Q9, Q10, Q11, Q12, Q13, Q14, Q15, Q16, Q17, Q18, Q19, Q20, Q21, Q22, Q23, Q24, Q25, Q26, Q27, Q28, Q29, Q30, Q31, Q32, Q33]), "operationType" : NewBodyOperationType.REMOVE, "endBound" : BoundingType.UP_TO_SURFACE, "oppositeDirection" : true, "endBoundEntityFace" : qUnion([Q34]), "depth" : 25 * mm});
        }
    });
